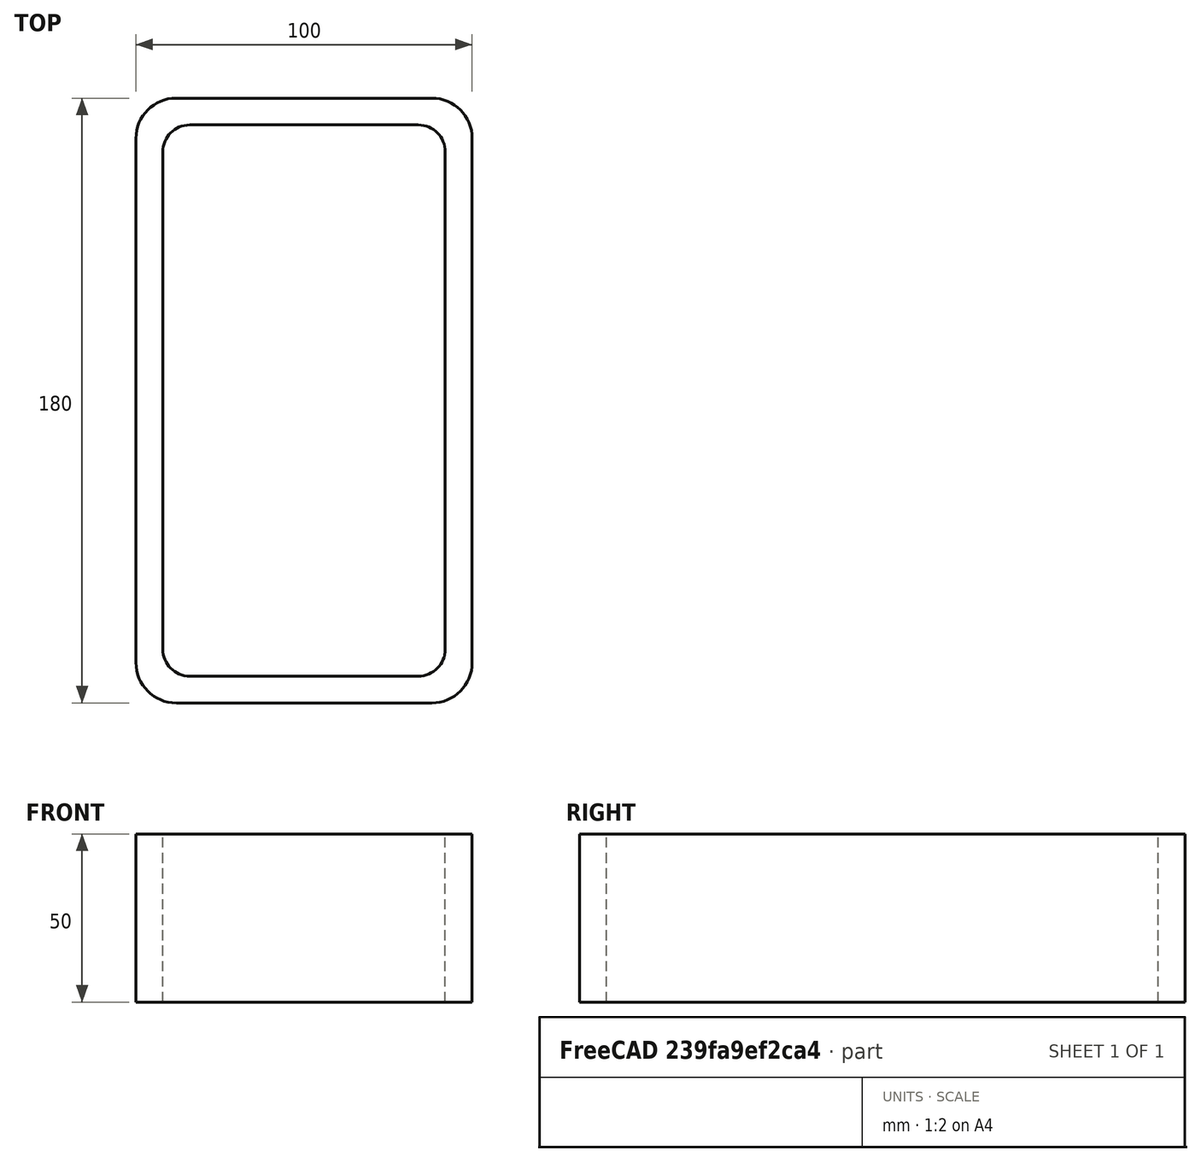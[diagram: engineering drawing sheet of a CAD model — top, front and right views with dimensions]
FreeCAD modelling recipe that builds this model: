
FCSTD DOCUMENT  (FreeCAD 0.15R4671 (Git))
Label: Rectangular hollow section 180x100x8 EN10219 S235JRH
License: All rights reserved
LicenseURL: http://en.wikipedia.org/wiki/All_rights_reserved
objects: Sketcher::SketchObject×1, Part::Extrusion×1
note: 2 computed .brp shape members not serialized (recipe doc carries the construction recipe); baked Part::Feature solids carry a one-line shape summary decoded from their .brp

FEATURE [Sketcher::SketchObject] Sketch
  sketch-geometry (16):
    g0: LineSegment StartX=-34 StartY=82 StartZ=0 EndX=34 EndY=82 EndZ=0
    g1: LineSegment StartX=42 StartY=74 StartZ=0 EndX=42 EndY=-74 EndZ=0
    g2: LineSegment StartX=34 StartY=-82 StartZ=0 EndX=-34 EndY=-82 EndZ=0
    g3: LineSegment StartX=-42 StartY=-74 StartZ=0 EndX=-42 EndY=74 EndZ=0
    g4: LineSegment StartX=-38 StartY=90 StartZ=0 EndX=38 EndY=90 EndZ=0
    g5: LineSegment StartX=50 StartY=78 StartZ=0 EndX=50 EndY=-78 EndZ=0
    g6: LineSegment StartX=38 StartY=-90 StartZ=0 EndX=-38 EndY=-90 EndZ=0
    g7: LineSegment StartX=-50 StartY=-78 StartZ=0 EndX=-50 EndY=78 EndZ=0
    g8: ArcOfCircle CenterX=-34 CenterY=74 CenterZ=0 NormalX=0 NormalY=0 NormalZ=1 Radius=8 StartAngle=1.5708 EndAngle=3.14159
    g9: ArcOfCircle CenterX=34 CenterY=74 CenterZ=0 NormalX=0 NormalY=0 NormalZ=1 Radius=8 StartAngle=0 EndAngle=1.5708
    g10: ArcOfCircle CenterX=34 CenterY=-74 CenterZ=0 NormalX=0 NormalY=0 NormalZ=1 Radius=8 StartAngle=4.71239 EndAngle=6.28319
    g11: ArcOfCircle CenterX=-34 CenterY=-74 CenterZ=0 NormalX=0 NormalY=0 NormalZ=1 Radius=8 StartAngle=3.14159 EndAngle=4.71239
    g12: ArcOfCircle CenterX=38 CenterY=78 CenterZ=0 NormalX=0 NormalY=0 NormalZ=1 Radius=12 StartAngle=0 EndAngle=1.5708
    g13: ArcOfCircle CenterX=38 CenterY=-78 CenterZ=0 NormalX=0 NormalY=0 NormalZ=1 Radius=12 StartAngle=4.71239 EndAngle=6.28319
    g14: ArcOfCircle CenterX=-38 CenterY=-78 CenterZ=0 NormalX=0 NormalY=0 NormalZ=1 Radius=12 StartAngle=3.14159 EndAngle=4.71239
    g15: ArcOfCircle CenterX=-38 CenterY=78 CenterZ=0 NormalX=0 NormalY=0 NormalZ=1 Radius=12 StartAngle=1.5708 EndAngle=3.14159
  constraints (36):
    c: Horizontal(g2)
    c: Vertical(g3)
    c: Horizontal(g6)
    c: Vertical(g7)
    c: Tangent(g3,g8) = 1.5708
    c: Tangent(g0,g8) = 1.5708
    c: Tangent(g0,g9) = 1.5708
    c: Tangent(g1,g9) = 1.5708
    c: Tangent(g1,g10) = 1.5708
    c: Tangent(g2,g10) = 1.5708
    c: Tangent(g2,g11) = 1.5708
    c: Tangent(g3,g11) = 1.5708
    c: Tangent(g4,g12) = 1.5708
    c: Tangent(g5,g12) = 1.5708
    c: Tangent(g5,g13) = 1.5708
    c: Tangent(g6,g13) = 1.5708
    c: Tangent(g6,g14) = 1.5708
    c: Tangent(g7,g14) = 1.5708
    c: Tangent(g7,g15) = 1.5708
    c: Tangent(g4,g15) = 1.5708
    c: Equal(g9,g8)
    c: Equal(g9,g11)
    c: Equal(g9,g10)
    c: Equal(g12,g15)
    c: Equal(g12,g14)
    c: Equal(g12,g13)
    c: Symmetric(g4,g6,g-1)
    c: Symmetric(g7,g5,g-2)
    c: DistanceY(g4,g6) = -180
    c: DistanceX(g7,g5) = 100
    c: Symmetric(g3,g1,g-2)
    c: Symmetric(g0,g2,g-1)
    c: DistanceY(g0,g4) = 8
    c: DistanceX(g5,g1) = -8
    c: Radius(g9) = 8
    c: Radius(g12) = 12
FEATURE [Part::Extrusion] Extrude  label="Rectangular hollow section 180x100x8 EN10219 S235JRH"
  Base = -> Sketch
  Dir = (0,0,50)
  Solid = true
